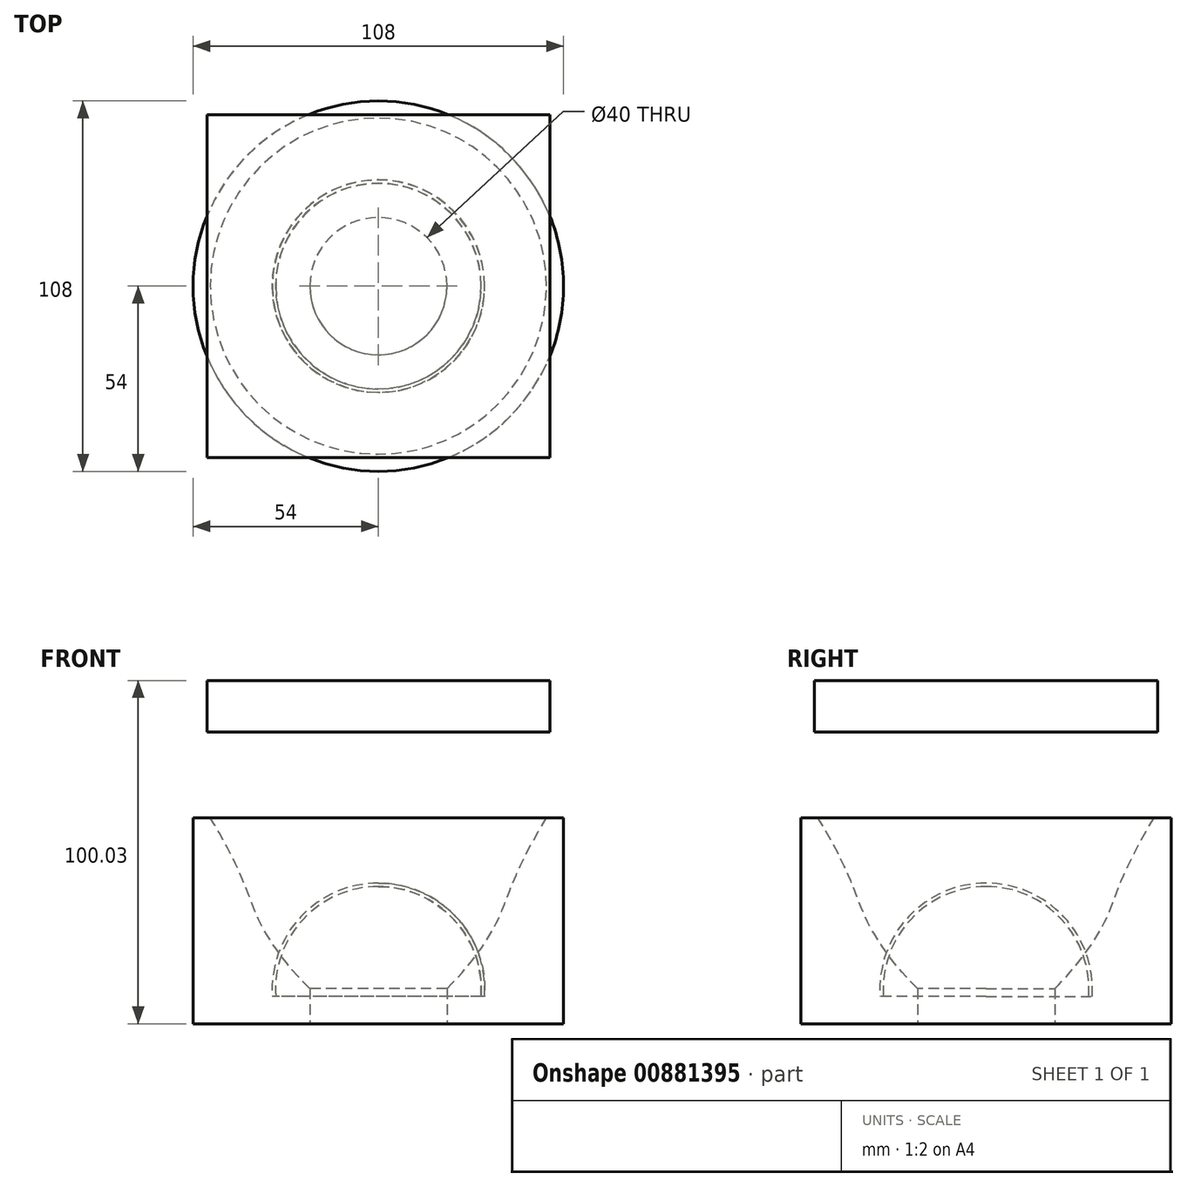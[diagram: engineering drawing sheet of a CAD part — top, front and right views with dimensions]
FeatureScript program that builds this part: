
annotation { "Feature Type Name" : "Feature", "Feature Type Description" : "" }
export const myFeature = defineFeature(function(context is Context, id is Id, definition is map)
    precondition{}
    {
        {
            var Q0;
            Q0=qCreatedBy(makeId("Front.planeOp"),FACE);
            var sketch = newSketch(context, id + "F0", { "sketchPlane" : qUnion([Q0])});
            skLineSegment(sketch, "E0", {"start": v(0, 150) * mm, "end": v(0, 0) * mm, "construction": true});
            skLineSegment(sketch, "E1.1.0.0", {"start": v(3.5, 150) * mm, "end": v(3.5, 0) * mm, "construction": true});
            skLineSegment(sketch, "E1.2.0.0", {"start": v(7, 150) * mm, "end": v(7, 0) * mm, "construction": true});
            skLineSegment(sketch, "E1.3.0.0", {"start": v(10.5, 150) * mm, "end": v(10.5, 0) * mm, "construction": true});
            skLineSegment(sketch, "E1.4.0.0", {"start": v(14, 150) * mm, "end": v(14, 0) * mm, "construction": true});
            skLineSegment(sketch, "E1.5.0.0", {"start": v(17.5, 150) * mm, "end": v(17.5, 0) * mm, "construction": true});
            skLineSegment(sketch, "E1.6.0.0", {"start": v(21, 150) * mm, "end": v(21, 0) * mm, "construction": true});
            skLineSegment(sketch, "E1.7.0.0", {"start": v(24.5, 150) * mm, "end": v(24.5, 0) * mm, "construction": true});
            skLineSegment(sketch, "E1.8.0.0", {"start": v(28, 150) * mm, "end": v(28, 0) * mm, "construction": true});
            skLineSegment(sketch, "E1.9.0.0", {"start": v(31.5, 150) * mm, "end": v(31.5, 0) * mm, "construction": true});
            skLineSegment(sketch, "E1.10.0.0", {"start": v(35, 150) * mm, "end": v(35, 0) * mm, "construction": true});
            skLineSegment(sketch, "E1.11.0.0", {"start": v(38.5, 150) * mm, "end": v(38.5, 0) * mm, "construction": true});
            skLineSegment(sketch, "E1.12.0.0", {"start": v(42, 150) * mm, "end": v(42, 0) * mm, "construction": true});
            skLineSegment(sketch, "E1.13.0.0", {"start": v(45.5, 150) * mm, "end": v(45.5, 0) * mm, "construction": true});
            skLineSegment(sketch, "E1.14.0.0", {"start": v(49, 150) * mm, "end": v(49, 0) * mm, "construction": true});
            skLineSegment(sketch, "E1.direction1", {"start": v(0, 0) * mm, "end": v(3.5, 0) * mm, "construction": true});
            skLineSegment(sketch, "E2", {"start": v(3.5, 0.3) * mm, "end": v(-7.32, 0.3) * mm, "construction": true});
            skLineSegment(sketch, "E3", {"start": v(7, 1.23) * mm, "end": v(-9.26, 1.23) * mm, "construction": true});
            skLineSegment(sketch, "E4", {"start": v(10.5, 2.76) * mm, "end": v(-7.21, 2.76) * mm, "construction": true});
            skLineSegment(sketch, "E5", {"start": v(14, 4.9) * mm, "end": v(-11.22, 4.9) * mm, "construction": true});
            skLineSegment(sketch, "E6", {"start": v(35, 30.62) * mm, "end": v(-16.71, 30.62) * mm, "construction": true});
            skLineSegment(sketch, "E7", {"start": v(24.5, 15) * mm, "end": v(-54.75, 15) * mm, "construction": true});
            skLineSegment(sketch, "E8", {"start": v(49, 60.02) * mm, "end": v(-55.05, 60.02) * mm, "construction": true});
            skLineSegment(sketch, "E9", {"start": v(54, 0) * mm, "end": v(54, 60.02) * mm});
            skLineSegment(sketch, "E10", {"start": v(54, 60.02) * mm, "end": v(49, 60.02) * mm});
            skLineSegment(sketch, "E11", {"start": v(3.5, 0.3) * mm, "end": v(3.5, 0) * mm});
            skLineSegment(sketch, "E12", {"start": v(54, 0) * mm, "end": v(7, 0) * mm});
            skLineSegment(sketch, "E13", {"start": v(7, 0) * mm, "end": v(7, 1.23) * mm});
            skFitSpline(sketch, "E14", {"points": [v(0, 0) * mm, v(3.5, 0.3) * mm, v(7, 1.23) * mm, v(10.5, 2.76) * mm, v(14, 4.9) * mm, v(24.5, 15) * mm, v(35, 30.62) * mm, v(49, 60.02) * mm], "startDerivative": vector(81.21, 0) * mm, "endDerivative": vector(112.73, 185.58) * mm});
            skSolve(sketch);
        }
        {
            var Q0;
            Q0 = qSketchRegion(id + "F0", true);
            var Q1;
            Q1=sQuery(id+"F0.wireOp",EDGE,"E0");
            revolve(context, id + "F1", {"surfaceOperationType" : NewSurfaceOperationType.NEW, "entities" : qUnion([Q0]), "axis" : qUnion([Q1]), "revolveType" : RevolveType.FULL});
        }
        {
            var Q0;
            Q0=makeQuery(id+"F1.opRevolve","SWEPT_FACE",FACE,{"disambiguationData":[OSD([sQuery(id+"F0.wireOp",EDGE,"E12")])]});
            var sketch = newSketch(context, id + "F2", { "sketchPlane" : qUnion([Q0])});
            skCircle(sketch, "E15", {"center": v(0, 0) * mm, "radius": 20 * mm});
            skSolve(sketch);
        }
        {
            var Q0;
            Q0 = qSketchRegion(id + "F2", true);
            extrude(context, id + "F3", {"entities" : qUnion([Q0]), "operationType" : NewBodyOperationType.REMOVE, "endBound" : BoundingType.THROUGH_ALL, "oppositeDirection" : true, "depth" : 25 * mm, "offsetDistance" : 25 * mm});
        }
        {
            var Q0;
            Q0=makeQuery(id+"F1.opRevolve","SWEPT_FACE",FACE,{"disambiguationData":[OSD([sQuery(id+"F0.wireOp",EDGE,"E12")])]});
            var sketch = newSketch(context, id + "F4", { "sketchPlane" : qUnion([Q0])});
            skCircle(sketch, "E16", {"center": v(0, 0) * mm, "radius": 164.62 * mm});
            skSolve(sketch);
        }
        {
            var Q0;
            Q0=makeQuery(id+"FioQlqe0oa64Gp2_1.boolean.opBoolean","COPY",FACE,{"derivedFrom":makeQuery(id+"FioQlqe0oa64Gp2_1.opExtrude","CAP_FACE",FACE,{"disambiguationData":[OSD([sQuery(id+"F4.wireOp",EDGE,"E16")])],"isStart":false})});
            var sketch = newSketch(context, id + "F5", { "sketchPlane" : qUnion([Q0])});
            skCircle(sketch, "E17", {"center": v(0, 0) * mm, "radius": 30 * mm});
            skSolve(sketch);
        }
        {
            var Q0;
            Q0=qCreatedBy(makeId("Front.planeOp"),FACE);
            var sketch = newSketch(context, id + "F6", { "sketchPlane" : qUnion([Q0])});
            skArc(sketch, "E18", {"start": v(0, 40) * mm, "mid": v(-21.92, 30.48) * mm, "end": v(-29.93, 7.97) * mm});
            skArc(sketch, "E19", {"start": v(0, 41) * mm, "mid": v(-22.63, 31.19) * mm, "end": v(-30.93, 7.97) * mm});
            skLineSegment(sketch, "E20", {"start": v(0, 40) * mm, "end": v(0, 41) * mm});
            skLineSegment(sketch, "E21", {"start": v(-29.93, 7.97) * mm, "end": v(-30.93, 7.97) * mm});
            skLineSegment(sketch, "E22", {"start": v(0, 0) * mm, "end": v(0, 47.27) * mm, "construction": true});
            skSolve(sketch);
        }
        {
            var Q0;
            Q0 = qSketchRegion(id + "F6", true);
            var Q1;
            Q1=sQuery(id+"F6.wireOp",EDGE,"E22");
            revolve(context, id + "F7", {"surfaceOperationType" : NewSurfaceOperationType.NEW, "entities" : qUnion([Q0]), "axis" : qUnion([Q1]), "revolveType" : RevolveType.FULL});
        }
        {
            var Q0;
            Q0=makeQuery(id+"F4HlaZHBmJPrRmO_1.boolean.opBoolean","SPLIT",FACE,{"disambiguationData":[TD([makeQuery(id+"F4HlaZHBmJPrRmO_1.opExtrude","CAP_FACE",FACE,{"disambiguationData":[OSD([sQuery(id+"FO8Jd8klc5X31Js_1.wireOp",EDGE,"JOtJLLj6-ss0n-O58n-9PQQ-F9Yoiz3CMyKa.bottom"),sQuery(id+"FO8Jd8klc5X31Js_1.wireOp",EDGE,"JOtJLLj6-ss0n-O58n-9PQQ-F9Yoiz3CMyKa.top"),sQuery(id+"FO8Jd8klc5X31Js_1.wireOp",EDGE,"JOtJLLj6-ss0n-O58n-9PQQ-F9Yoiz3CMyKa.left"),sQuery(id+"FO8Jd8klc5X31Js_1.wireOp",EDGE,"JOtJLLj6-ss0n-O58n-9PQQ-F9Yoiz3CMyKa.right")])],"isStart":true})])],"derivedFrom":makeQuery(id+"F1.opRevolve","SWEPT_FACE",FACE,{"disambiguationData":[OSD([sQuery(id+"F0.wireOp",EDGE,"E10")])]})});
            cPlane(context, id + "F8", {"entities" : qUnion([Q0]), "cplaneType" : CPlaneType.OFFSET, "offset" : 25 * mm, "width" : 150 * mm, "height" : 150 * mm});
        }
        {
            var Q0;
            Q0=qCreatedBy(id+"F8.planeOp",FACE);
            var sketch = newSketch(context, id + "F9", { "sketchPlane" : qUnion([Q0])});
            skLineSegment(sketch, "E23.bottom", {"start": v(-50, -50) * mm, "end": v(50, -50) * mm});
            skLineSegment(sketch, "E23.top", {"start": v(-50, 50) * mm, "end": v(50, 50) * mm});
            skLineSegment(sketch, "E23.left", {"start": v(-50, -50) * mm, "end": v(-50, 50) * mm});
            skLineSegment(sketch, "E23.right", {"start": v(50, -50) * mm, "end": v(50, 50) * mm});
            skSolve(sketch);
        }
        {
            var Q0;
            Q0=makeQuery(id+"F9.imprint","IMPRINT",FACE,{"disambiguationData":[TD([[makeQuery(id+"F9.imprint","IMPRINT",EDGE,{"derivedFrom":sQuery(id+"F9.wireOp",EDGE,"E23.bottom")}),1.0]])]});
            extrude(context, id + "F10", {"entities" : qUnion([Q0]), "depth" : 15 * mm, "offsetDistance" : 25 * mm});
        }
    });
